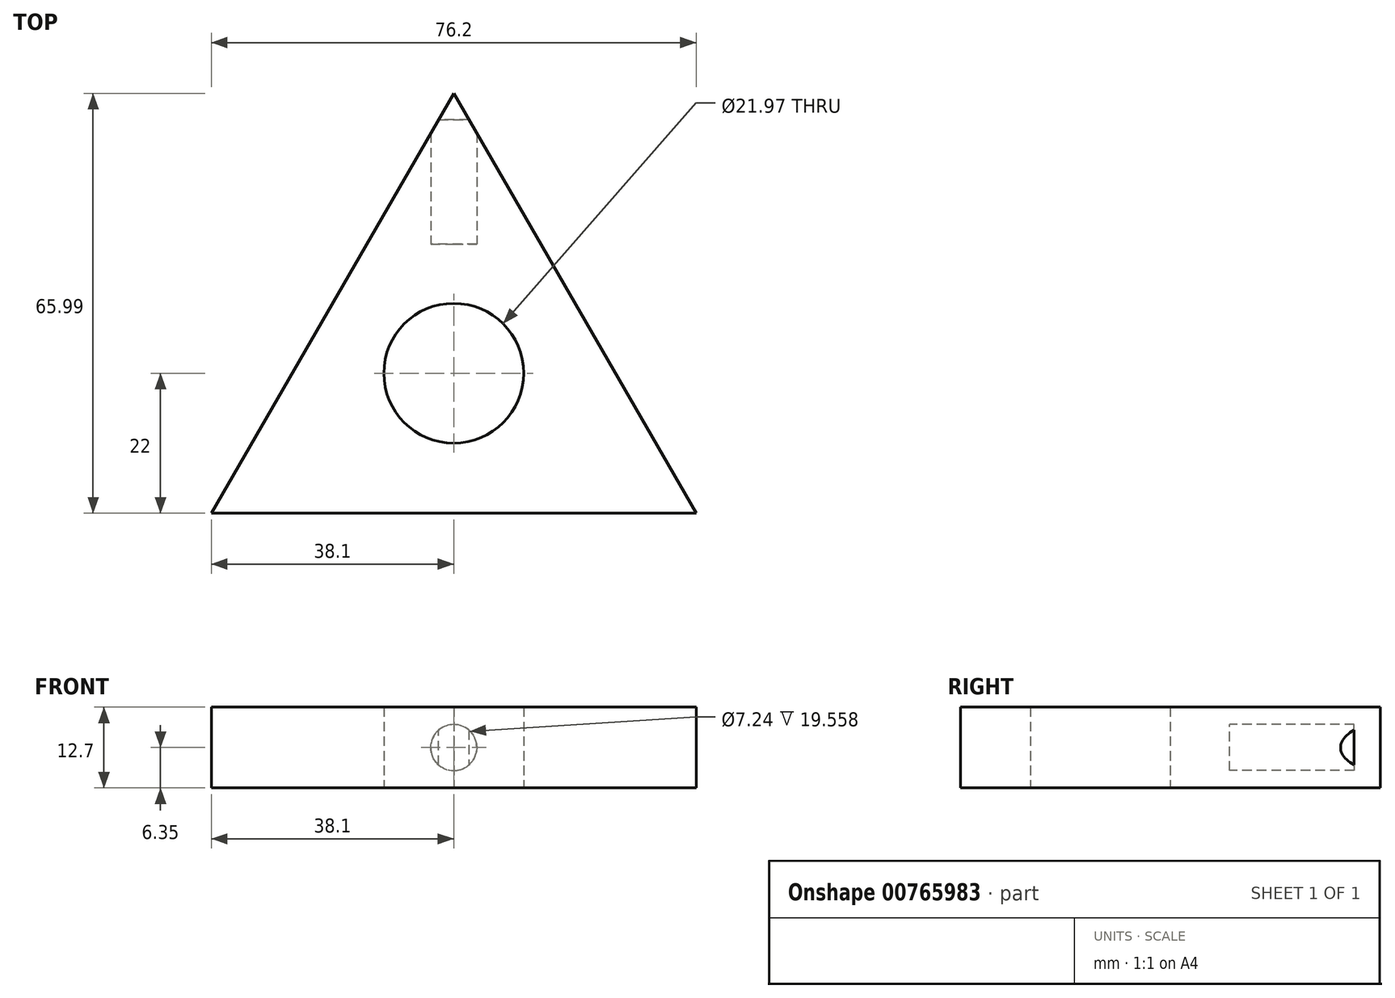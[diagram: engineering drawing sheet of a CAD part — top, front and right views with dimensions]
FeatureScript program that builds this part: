
annotation { "Feature Type Name" : "Feature", "Feature Type Description" : "" }
export const myFeature = defineFeature(function(context is Context, id is Id, definition is map)
    precondition{}
    {
        {
            var Q0;
            Q0=qCreatedBy(makeId("Top.planeOp"),FACE);
            var sketch = newSketch(context, id + "F0", { "sketchPlane" : qUnion([Q0])});
            skCircle(sketch, "E0.cCircle", {"center": v(0, 0) * mm, "radius": 44 * mm, "construction": true});
            skLineSegment(sketch, "E0.0", {"start": v(0, 44) * mm, "end": v(38.1, -22) * mm});
            skLineSegment(sketch, "E0.1", {"start": v(38.1, -22) * mm, "end": v(-38.1, -22) * mm});
            skLineSegment(sketch, "E0.2", {"start": v(-38.1, -22) * mm, "end": v(0, 44) * mm});
            skCircle(sketch, "E1", {"center": v(0, 0) * mm, "radius": 10.99 * mm});
            skSolve(sketch);
        }
        {
            var Q0;
            Q0=qCreatedBy(makeId("Front.planeOp"),FACE);
            cPlane(context, id + "F1", {"entities" : qUnion([Q0]), "cplaneType" : CPlaneType.OFFSET, "offset" : 20.32 * mm, "oppositeDirection" : true, "width" : 152.4 * mm, "height" : 152.4 * mm});
        }
        {
            var Q0;
            Q0=qCreatedBy(id+"F1.planeOp",FACE);
            var sketch = newSketch(context, id + "F2", { "sketchPlane" : qUnion([Q0])});
            skCircle(sketch, "E2", {"center": v(0, 0) * mm, "radius": 3.62 * mm});
            skSolve(sketch);
        }
        {
            var Q0;
            Q0=makeQuery(id+"F0.imprint","IMPRINT",FACE,{"disambiguationData":[TD([[makeQuery(id+"F0.imprint","IMPRINT",EDGE,{"derivedFrom":sQuery(id+"F0.wireOp",EDGE,"E0.0")}),-1.0]])]});
            extrude(context, id + "F3", {"entities" : qUnion([Q0]), "endBound" : BoundingType.SYMMETRIC, "depth" : 12.7 * mm, "offsetDistance" : 25.4 * mm});
        }
        {
            var Q0;
            Q0 = qSketchRegion(id + "F2", true);
            var Q1;
            Q1=sQuery(id+"F2.wireOp",EDGE,"E2");
            extrude(context, id + "F4", {"entities" : qUnion([Q0]), "operationType" : NewBodyOperationType.REMOVE, "surfaceEntities" : qUnion([Q1]), "oppositeDirection" : true, "depth" : 19.56 * mm, "offsetDistance" : 25.4 * mm});
        }
    });
